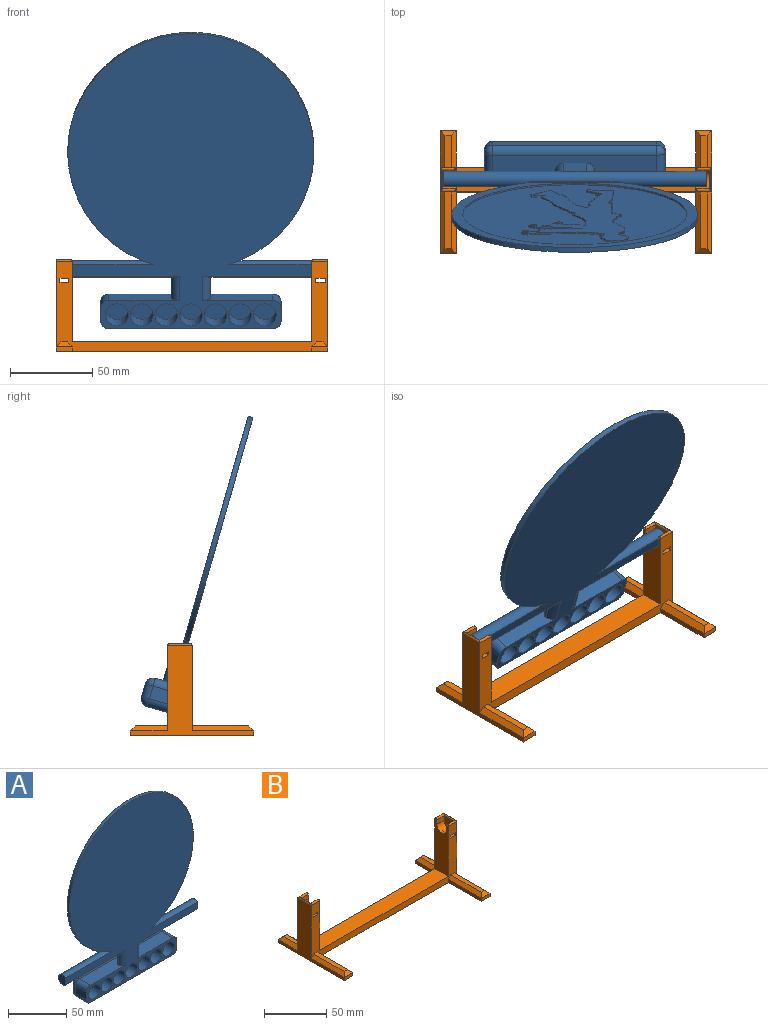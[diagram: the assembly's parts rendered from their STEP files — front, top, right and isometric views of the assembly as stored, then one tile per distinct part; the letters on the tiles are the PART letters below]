
ASSEMBLY  parts=2 mates=1
PART A: 155 faces, bbox 160x18.5x187 mm
  f0: plane 136.71x136.71mm, normal (0,1,0), area 11719.2mm2, adj f2,f3,f4,f5,f6,f7,f8,f9
  f1: extruded ~2.51x1.6mm, area 3.6mm2, adj f108,f109,f110
  f2: plane 1.01x1mm, normal (1,0,0.07), area 1mm2, adj f0,f3,f107,f109
  f3: plane 1.51x1.02mm, normal (0.83,0,-0.56), area 1.8mm2, adj f0,f2,f4,f109
  f4: extruded ~28.46x6.31mm, area 33.3mm2, adj f0,f3,f5,f109
  f5: plane 3.77x2.31mm, normal (0.85,0,-0.52), area 4.4mm2, adj f0,f4,f6,f109
  f6: plane 1.51x1mm, normal (1,0,-0.01), area 1.5mm2, adj f0,f5,f7,f109
  f7: extruded ~15.79x5.36mm, area 19.1mm2, adj f0,f6,f8,f109
  f8: plane 2.62x1mm, normal (0.26,0,-0.96), area 2.7mm2, adj f0,f7,f9,f109
  f9: plane 1.24x1mm, normal (1,0,-0.03), area 1.2mm2, adj f0,f8,f10,f109
  f10: extruded ~2.49x1mm, area 2.5mm2, adj f0,f9,f11,f109
  f11: plane 1.25x1mm, normal (0.98,0,0.2), area 1.3mm2, adj f0,f10,f12,f109
  f12: plane 1x0.59mm, normal (0.89,0,-0.45), area 0.7mm2, adj f0,f11,f13,f109
  f13: extruded ~3.39x1mm, area 3.4mm2, adj f0,f12,f14,f109
  f14: plane 2.8x1mm, normal (1,0,-0.03), area 2.8mm2, adj f0,f13,f15,f109
  f15: plane 1x0.68mm, normal (0.87,0,0.5), area 0.8mm2, adj f0,f14,f16,f109
  f16: extruded ~2.68x1mm, area 3.6mm2, adj f0,f15,f17,f109
  f17: plane 1x0.52mm, normal (0.88,0,0.47), area 0.6mm2, adj f0,f16,f18,f109
  f18: plane 1.3x1mm, normal (0.97,0,-0.23), area 1.3mm2, adj f0,f17,f19,f109
  f19: extruded ~3.57x1mm, area 3.6mm2, adj f0,f18,f20,f109
  f20: plane 2.27x1mm, normal (1,0,-0.03), area 2.3mm2, adj f0,f19,f21,f109
  f21: plane 1x0.44mm, normal (0.15,0,-0.99), area 0.4mm2, adj f0,f20,f22,f109
  f22: extruded ~20.57x2.97mm, area 24.5mm2, adj f0,f21,f23,f109
  f23: plane 1x0.49mm, normal (0.99,0,0.16), area 0.5mm2, adj f0,f22,f24,f109
  f24: plane 1x0.47mm, normal (-0.16,0,-0.99), area 0.5mm2, adj f0,f23,f25,f109
  f25: plane 1x0.47mm, normal (-0.16,0,-0.99), area 0.5mm2, adj f0,f24,f26,f109
  f26: plane 1x0.47mm, normal (0.99,0,0.15), area 0.5mm2, adj f0,f25,f27,f109
  f27: extruded ~6.73x1mm, area 6.8mm2, adj f0,f26,f28,f109
  f28: plane 1x0.6mm, normal (0.99,0,0.14), area 0.6mm2, adj f0,f27,f29,f109
  f29: plane 1x0.65mm, normal (0,0,-1), area 0.6mm2, adj f0,f28,f30,f109
  f30: extruded ~14.23x1.47mm, area 14.4mm2, adj f0,f29,f31,f109
  f31: plane 1x0mm, normal (0.19,0,-0.98), area 0mm2, adj f0,f30,f32,f109
  f32: extruded ~7.88x7.34mm, area 12.7mm2, adj f0,f31,f33,f109
  f33: plane 1.29x1.13mm, normal (-0.66,0,0.75), area 1.7mm2, adj f0,f32,f34,f109
  f34: plane 1.58x1mm, normal (-1,0,0), area 1.6mm2, adj f0,f33,f35,f109
  f35: plane 1x0.57mm, normal (-0.15,0,-0.99), area 0.6mm2, adj f0,f34,f36,f109
  f36: extruded ~17.24x6.28mm, area 24.4mm2, adj f0,f35,f37,f109
  f37: plane 1x0.44mm, normal (-0.54,0,-0.84), area 0.5mm2, adj f0,f36,f38,f109
  f38: plane 1x0.97mm, normal (-1,0,0), area 1mm2, adj f0,f37,f39,f109
  f39: extruded ~5.62x1mm, area 5.7mm2, adj f0,f38,f40,f109
  f40: plane 1x0.38mm, normal (-0.81,0,0.58), area 0.5mm2, adj f0,f39,f41,f109
  f41: plane 1x0.73mm, normal (-0.89,0,-0.45), area 0.8mm2, adj f0,f40,f42,f109
  f42: extruded ~2.83x1mm, area 3mm2, adj f0,f41,f43,f109
  f43: plane 2.1x1mm, normal (-0.97,0,-0.25), area 2.2mm2, adj f0,f42,f44,f109
  f44: plane 1x0.35mm, normal (0.63,0,-0.78), area 0.4mm2, adj f0,f43,f45,f109
  f45: extruded ~3.66x3.24mm, area 4.9mm2, adj f0,f44,f46,f109
  f46: plane 3.32x2.96mm, normal (0.67,0,-0.75), area 4.4mm2, adj f0,f45,f47,f109
  f47: plane 1.7x1mm, normal (0.95,0,-0.32), area 1.8mm2, adj f0,f46,f48,f109
  f48: extruded ~14.76x4.58mm, area 15.5mm2, adj f0,f47,f49,f109
  f49: plane 1.73x1mm, normal (0.99,0,-0.12), area 1.7mm2, adj f0,f48,f50,f109
  f50: plane 1x0.47mm, normal (0.29,0,-0.96), area 0.5mm2, adj f0,f49,f51,f109
  f51: extruded ~21.49x12.9mm, area 34.8mm2, adj f0,f50,f52,f109
  f52: plane 1x0.57mm, normal (-0.69,0,0.72), area 0.8mm2, adj f0,f51,f53,f109
  f53: plane 1.11x1mm, normal (0.05,0,1), area 1.1mm2, adj f0,f52,f54,f109
  f54: extruded ~5.49x1.15mm, area 5.6mm2, adj f0,f53,f55,f109
  f55: plane 1x0.6mm, normal (0.2,0,0.98), area 0.6mm2, adj f0,f54,f56,f109
  f56: plane 1x0.58mm, normal (-0.78,0,0.62), area 0.7mm2, adj f0,f55,f57,f109
  f57: extruded ~41.71x20.66mm, area 50.6mm2, adj f0,f56,f58,f109
  f58: plane 1x0.34mm, normal (-0.81,0,-0.59), area 0.4mm2, adj f0,f57,f59,f109
  f59: plane 1.33x1.14mm, normal (-0.76,0,0.65), area 1.7mm2, adj f0,f58,f60,f109
  f60: extruded ~20.97x6.82mm, area 22.8mm2, adj f0,f59,f61,f109
  f61: plane 2.21x1mm, normal (-1,0,-0.04), area 2.2mm2, adj f0,f60,f62,f109
  f62: plane 6.06x1.23mm, normal (0.2,0,-0.98), area 6.2mm2, adj f0,f61,f63,f109
  f63: extruded ~8.45x1.9mm, area 11.1mm2, adj f0,f62,f64,f109
  f64: plane 1.79x1mm, normal (0.99,0,-0.13), area 1.8mm2, adj f0,f63,f65,f109
  f65: plane 1.25x1.17mm, normal (-0.73,0,-0.68), area 1.7mm2, adj f0,f64,f66,f109
  f66: plane 1.25x1.17mm, normal (-0.73,0,-0.68), area 1.7mm2, adj f0,f65,f67,f109
  f67: plane 1x0.76mm, normal (1,0,0), area 0.8mm2, adj f0,f66,f68,f109
  f68: extruded ~2.98x2.17mm, area 3.8mm2, adj f0,f67,f69,f109
  f69: plane 1.1x1.01mm, normal (0.74,0,0.68), area 1.5mm2, adj f0,f68,f70,f109
  f70: plane 2.29x1.07mm, normal (-0.42,0,-0.91), area 2.5mm2, adj f0,f69,f71,f109
  f71: extruded ~2.97x2.11mm, area 5.9mm2, adj f0,f70,f72,f109
  f72: plane 1.89x1.5mm, normal (0.78,0,0.62), area 2.4mm2, adj f0,f71,f73,f109
  f73: plane 2.09x2.07mm, normal (-0.7,0,-0.71), area 2.9mm2, adj f0,f72,f74,f109
  f74: plane 2.09x2.07mm, normal (-0.7,0,-0.71), area 2.9mm2, adj f0,f73,f75,f109
  f75: plane 2.14x1mm, normal (-0.93,0,-0.37), area 2.3mm2, adj f0,f74,f76,f109
  f76: plane 2.14x1mm, normal (-0.93,0,-0.37), area 2.3mm2, adj f0,f75,f77,f109
  f77: plane 2.02x1mm, normal (-0.02,0,-1), area 2mm2, adj f0,f76,f78,f109
  f78: plane 2.02x1mm, normal (-0.02,0,-1), area 2mm2, adj f0,f77,f79,f109
  f79: plane 1x0.46mm, normal (0.74,0,-0.67), area 0.6mm2, adj f0,f78,f80,f109
  f80: plane 1x0.46mm, normal (0.74,0,-0.67), area 0.6mm2, adj f0,f79,f81,f109
  f81: plane 2.17x1mm, normal (-0.06,0,-1), area 2.2mm2, adj f0,f80,f82,f109
  f82: plane 1x0.66mm, normal (0.69,0,-0.72), area 0.9mm2, adj f0,f81,f83,f109
  f83: extruded ~2.49x1.39mm, area 4.9mm2, adj f0,f82,f84,f109
  f84: plane 1x0.32mm, normal (-0.68,0,0.73), area 0.4mm2, adj f0,f83,f85,f109
  f85: extruded ~1x0.97mm, area 1.5mm2, adj f0,f84,f86,f109
  f86: extruded ~4.32x3.43mm, area 16.4mm2, adj f0,f85,f87,f109
  f87: extruded ~10.21x4.43mm, area 17.1mm2, adj f0,f86,f88,f109
  f88: plane 2.83x1mm, normal (0.05,0,1), area 2.8mm2, adj f0,f87,f89,f109
  f89: plane 9.14x1.69mm, normal (-0.18,0,0.98), area 9.3mm2, adj f0,f88,f90,f109
  f90: extruded ~9.78x2.05mm, area 10mm2, adj f0,f89,f91,f109
  f91: plane 1x0.64mm, normal (-0.49,0,0.87), area 0.7mm2, adj f0,f90,f92,f109
  f92: plane 2.67x1mm, normal (-0.17,0,-0.99), area 2.7mm2, adj f0,f91,f93,f109
  f93: plane 2.67x1mm, normal (-0.17,0,-0.99), area 2.7mm2, adj f0,f92,f94,f109
  f94: plane 3.34x1mm, normal (0.07,0,-1), area 3.3mm2, adj f0,f93,f95,f109
  f95: extruded ~4.88x1mm, area 4.9mm2, adj f0,f94,f96,f109
  f96: plane 1.55x1mm, normal (0.25,0,-0.97), area 1.6mm2, adj f0,f95,f97,f109
  f97: plane 1x0.82mm, normal (-0.38,0,-0.93), area 0.9mm2, adj f0,f96,f98,f109
  f98: extruded ~10.96x2.4mm, area 26.2mm2, adj f0,f97,f99,f109
  f99: plane 2.29x1mm, normal (-0.96,0,0.27), area 2.4mm2, adj f0,f98,f100,f109
  f100: plane 1.23x1mm, normal (-0.91,0,-0.42), area 1.4mm2, adj f0,f99,f101,f109
  f101: extruded ~4.04x1.19mm, area 4.8mm2, adj f0,f100,f102,f109
  f102: plane 1.31x1mm, normal (-0.17,0,-0.99), area 1.3mm2, adj f0,f101,f103,f109
  f103: plane 1x0.85mm, normal (0.48,0,-0.88), area 1mm2, adj f0,f102,f104,f109
  f104: extruded ~6.72x4.49mm, area 26.5mm2, adj f0,f103,f105,f109
  f105: plane 1.4x1mm, normal (-0.29,0,0.96), area 1.5mm2, adj f0,f104,f106,f109
  f106: plane 1.08x1mm, normal (0.23,0,0.97), area 1.1mm2, adj f0,f105,f107,f109
  f107: extruded ~59.88x19.13mm, area 85.7mm2, adj f0,f2,f106,f109
  f108: extruded ~2.43x1.73mm, area 3.6mm2, adj f1,f109,f110
  f109: plane 113.06x64.97mm, normal (0,1,0), area 2925.1mm2, adj f1,f2,f3,f4,f5,f6,f7,f8
  f110: plane 2.58x2.09mm, normal (0,1,0), area 1.3mm2, adj f1,f108
  f111: plane 150x144.11mm, normal (0,1,0), area 2762.3mm2, adj f112,f139,f140
  f112: cylinder r=68.35mm len=136.71mm, axis (0,-1,0), area 429.5mm2, adj f0,f111
  f113: plane 100x8mm, normal (0,1,0), area 800mm2, adj f148,f149,f152,f153
  f114: plane 14x14mm, normal (0,-1,0), area 153.9mm2, adj f127
  f115: plane 14x14mm, normal (0,-1,0), area 153.9mm2, adj f128
  f116: plane 14x14mm, normal (0,-1,0), area 153.9mm2, adj f129
  f117: plane 14x14mm, normal (0,-1,0), area 153.9mm2, adj f130
  f118: plane 14x14mm, normal (0,-1,0), area 153.9mm2, adj f131
  f119: plane 14x14mm, normal (0,-1,0), area 153.9mm2, adj f132
  f120: plane 14x14mm, normal (0,-1,0), area 153.9mm2, adj f133
  f121: cylinder r=5mm len=13.5mm, axis (0,-1,0), area 106mm2, adj f122,f126,f137,f151
  f122: plane 13.5x8mm, normal (1,0,0), area 108mm2, adj f121,f137,f145,f149
  f123: plane 100x13.5mm, normal (0,0,-1), area 1350mm2, adj f137,f145,f147,f148
  f124: plane 13.5x8mm, normal (-1,0,0), area 108mm2, adj f125,f137,f147,f152
  f125: cylinder r=5mm len=13.5mm, axis (0,-1,0), area 106mm2, adj f124,f126,f137,f154
  f126: plane 100x13.5mm, normal (0,0,1), area 1167.4mm2, adj f121,f125,f135,f137,f141,f142,f143,f144
  f127: cylinder r=7mm len=14mm, axis (0,-1,0), area 615.8mm2, adj f114,f137
  f128: cylinder r=7mm len=14mm, axis (0,-1,0), area 615.8mm2, adj f115,f137
  f129: cylinder r=7mm len=14mm, axis (0,-1,0), area 615.8mm2, adj f116,f137
  f130: cylinder r=7mm len=14mm, axis (0,-1,0), area 615.8mm2, adj f117,f137
  f131: cylinder r=7mm len=14mm, axis (0,-1,0), area 615.8mm2, adj f118,f137
  f132: cylinder r=7mm len=14mm, axis (0,-1,0), area 615.8mm2, adj f119,f137
  f133: cylinder r=7mm len=14mm, axis (0,-1,0), area 615.8mm2, adj f120,f137
  f134: plane 10x8.5mm, normal (-1,0,0), area 71.2mm2, adj f137,f138
  f135: plane 19x14mm, normal (0,1,0), area 266mm2, adj f126,f138,f141,f143
  f136: plane 10x8.5mm, normal (1,0,0), area 71.2mm2, adj f137,f138
  f137: plane 187x160mm, normal (0,-1,0), area 19801.7mm2, adj f121,f122,f123,f124,f125,f126,f127,f128
  f138: cylinder r=5mm len=160mm, axis (-1,0,0), area 3296.6mm2, adj f134,f135,f136,f137,f139,f140,f141,f142
  f139: cylinder r=75mm len=150mm, axis (0,-1,0), area 1259.5mm2, adj f111,f137,f138,f140
  f140: plane 58.29x0.92mm, normal (0,0.73,0.68), area 69.2mm2, adj f111,f138,f139
  f141: cylinder r=5mm len=19mm, axis (0,0,-1), area 113.7mm2, adj f126,f135,f138,f142
  f142: cylinder r=5mm len=15.43mm, axis (0,0,1), area 103.9mm2, adj f126,f137,f138,f141
  f143: cylinder r=5mm len=19mm, axis (0,0,1), area 113.7mm2, adj f126,f135,f138,f144
  f144: cylinder r=5mm len=15.43mm, axis (0,0,-1), area 103.9mm2, adj f126,f137,f138,f143
  f145: cylinder r=5mm len=13.5mm, axis (0,1,0), area 106mm2, adj f122,f123,f137,f146
  f146: sphere r=5mm, area 39.3mm2, adj f145,f148,f149
  f147: cylinder r=5mm len=13.5mm, axis (0,1,0), area 106mm2, adj f123,f124,f137,f150
  f148: cylinder r=5mm len=100mm, axis (1,0,0), area 785.4mm2, adj f113,f123,f146,f150
  f149: cylinder r=5mm len=8mm, axis (0,0,1), area 62.8mm2, adj f113,f122,f146,f151
  f150: sphere r=5mm, area 39.3mm2, adj f147,f148,f152
  f151: sphere r=5mm, area 39.3mm2, adj f121,f149,f153
  f152: cylinder r=5mm len=8mm, axis (0,0,-1), area 62.8mm2, adj f113,f124,f150,f154
  f153: cylinder r=5mm len=100mm, axis (-1,0,0), area 785.4mm2, adj f113,f126,f151,f154
  f154: sphere r=5mm, area 39.3mm2, adj f125,f152,f153
PART B: 60 faces, bbox 165.6x75x56 mm
  f0: plane 165.62x55mm, normal (0,-1,0), area 1843.2mm2, adj f5,f6,f7,f8,f9,f10,f19,f20
  f1: plane 165.62x55mm, normal (0,1,0), area 1843.2mm2, adj f5,f6,f7,f8,f9,f10,f17,f18
  f2: cylinder r=5.5mm len=11mm, axis (-1,0,0), area 146.9mm2, adj f3,f4,f9,f14
  f3: plane 8.5x4.54mm, normal (0,1,0), area 38.6mm2, adj f2,f9,f14,f49
  f4: plane 8.5x4.54mm, normal (0,-1,0), area 38.6mm2, adj f2,f9,f14,f50
  f5: plane 165.62x75mm, normal (0,0,-1), area 3684.3mm2, adj f0,f1,f6,f10,f16,f17,f20,f21
  f6: plane 75x55mm, normal (1,0,0), area 1005mm2, adj f0,f1,f5,f16,f21,f30,f37,f58
  f7: plane 49x15mm, normal (-1,0,0), area 637.5mm2, adj f0,f1,f8,f11,f12,f13,f54,f57
  f8: plane 145.62x15mm, normal (0,0,1), area 2184.3mm2, adj f0,f1,f7,f9
  f9: plane 49x15mm, normal (1,0,0), area 637.5mm2, adj f0,f1,f2,f3,f4,f8,f48,f51
  f10: plane 75x55mm, normal (-1,0,0), area 1005mm2, adj f0,f1,f5,f22,f27,f32,f36,f52
  f11: plane 8.5x4.54mm, normal (0,-1,0), area 38.6mm2, adj f7,f13,f15,f55
  f12: plane 8.5x4.54mm, normal (0,1,0), area 38.6mm2, adj f7,f13,f15,f56
  f13: cylinder r=5.5mm len=11mm, axis (-1,0,0), area 146.9mm2, adj f7,f11,f12,f15
  f14: plane 11x10.04mm, normal (1,0,0), area 97.5mm2, adj f2,f3,f4,f53
  f15: plane 11x10.04mm, normal (-1,0,0), area 97.5mm2, adj f11,f12,f13,f59
  f16: plane 10x3mm, normal (0,1,0), area 30mm2, adj f5,f6,f17,f38
  f17: plane 22.5x3mm, normal (-1,0,0), area 67.5mm2, adj f1,f5,f16,f39
  f18: plane 19.5x4mm, normal (0,0,1), area 78mm2, adj f1,f37,f38,f39
  f19: plane 34.5x4mm, normal (0,0,1), area 138mm2, adj f0,f28,f29,f30
  f20: plane 37.5x3mm, normal (-1,0,0), area 112.5mm2, adj f0,f5,f21,f28
  f21: plane 10x3mm, normal (0,-1,0), area 30mm2, adj f5,f6,f20,f29
  f22: plane 10x3mm, normal (0,1,0), area 30mm2, adj f5,f10,f24,f35
  f23: plane 19.5x4mm, normal (0,0,1), area 78mm2, adj f1,f34,f35,f36
  f24: plane 22.5x3mm, normal (1,0,0), area 67.5mm2, adj f1,f5,f22,f34
  f25: plane 37.5x3mm, normal (1,0,0), area 112.5mm2, adj f0,f5,f27,f31
  f26: plane 34.5x4mm, normal (0,0,1), area 138mm2, adj f0,f31,f32,f33
  f27: plane 10x3mm, normal (0,-1,0), area 30mm2, adj f5,f10,f25,f33
  f28: plane 37.5x3mm, normal (-0.71,0,0.71), area 152.7mm2, adj f0,f19,f20,f29
  f29: plane 10x3mm, normal (0,-0.71,0.71), area 29.7mm2, adj f19,f21,f28,f30
  f30: plane 37.5x3mm, normal (0.71,0,0.71), area 152.7mm2, adj f0,f6,f19,f29
  f31: plane 37.5x3mm, normal (0.71,0,0.71), area 152.7mm2, adj f0,f25,f26,f33
  f32: plane 37.5x3mm, normal (-0.71,0,0.71), area 152.7mm2, adj f0,f10,f26,f33
  f33: plane 10x3mm, normal (0,-0.71,0.71), area 29.7mm2, adj f26,f27,f31,f32
  f34: plane 22.5x3mm, normal (0.71,0,0.71), area 89.1mm2, adj f1,f23,f24,f35
  f35: plane 10x3mm, normal (0,0.71,0.71), area 29.7mm2, adj f22,f23,f34,f36
  f36: plane 22.5x3mm, normal (-0.71,0,0.71), area 89.1mm2, adj f1,f10,f23,f35
  f37: plane 22.5x3mm, normal (0.71,0,0.71), area 89.1mm2, adj f1,f6,f18,f38
  f38: plane 10x3mm, normal (0,0.71,0.71), area 29.7mm2, adj f16,f18,f37,f39
  f39: plane 22.5x3mm, normal (-0.71,0,0.71), area 89.1mm2, adj f1,f17,f18,f38
  f40: plane 15x5.43mm, normal (0,0,1), area 81.4mm2, adj f0,f1,f41,f43
  f41: plane 15x2.5mm, normal (-1,0,0), area 37.5mm2, adj f0,f1,f40,f42
  f42: plane 15x5.43mm, normal (0,0,-1), area 81.4mm2, adj f0,f1,f41,f43
  f43: plane 15x2.5mm, normal (1,0,0), area 37.5mm2, adj f0,f1,f40,f42
  f44: plane 15x2.5mm, normal (-1,0,0), area 37.5mm2, adj f0,f1,f45,f47
  f45: plane 15x6mm, normal (0,0,-1), area 90mm2, adj f0,f1,f44,f46
  f46: plane 15x2.5mm, normal (1,0,0), area 37.5mm2, adj f0,f1,f45,f47
  f47: plane 15x6mm, normal (0,0,1), area 90mm2, adj f0,f1,f44,f46
  f48: cylinder r=1mm len=2mm, axis (0,1,0), area 2mm2, adj f9,f49
  f49: cylinder r=1mm len=10mm, axis (1,0,0), area 27.9mm2, adj f0,f3,f48,f52,f53
  f50: cylinder r=1mm len=10mm, axis (-1,0,0), area 27.9mm2, adj f1,f4,f51,f52,f53
  f51: cylinder r=1mm len=2mm, axis (0,1,0), area 2mm2, adj f9,f50
  f52: cylinder r=1mm len=15mm, axis (0,1,0), area 19.2mm2, adj f10,f49,f50,f53
  f53: cylinder r=1mm len=12.5mm, axis (0,-1,0), area 15.2mm2, adj f14,f49,f50,f52
  f54: cylinder r=1mm len=2mm, axis (0,1,0), area 2mm2, adj f7,f55
  f55: cylinder r=1mm len=10mm, axis (-1,0,0), area 27.9mm2, adj f1,f11,f54,f58,f59
  f56: cylinder r=1mm len=10mm, axis (1,0,0), area 27.9mm2, adj f0,f12,f57,f58,f59
  f57: cylinder r=1mm len=2mm, axis (0,1,0), area 2mm2, adj f7,f56
  f58: cylinder r=1mm len=15mm, axis (0,1,0), area 19.2mm2, adj f6,f55,f56,f59
  f59: cylinder r=1mm len=12.5mm, axis (0,1,0), area 15.2mm2, adj f15,f55,f56,f58
PLACE A rot(axis=(1,0,0),16deg) t=(-6.02,2.69,9.25)mm
PLACE B t=(-6.21,2.69,9.25)mm fixed
MATE revolute B.f2 <-> A.f138  axis (-1,0,0) through (75.98,2.69,9.25)mm
